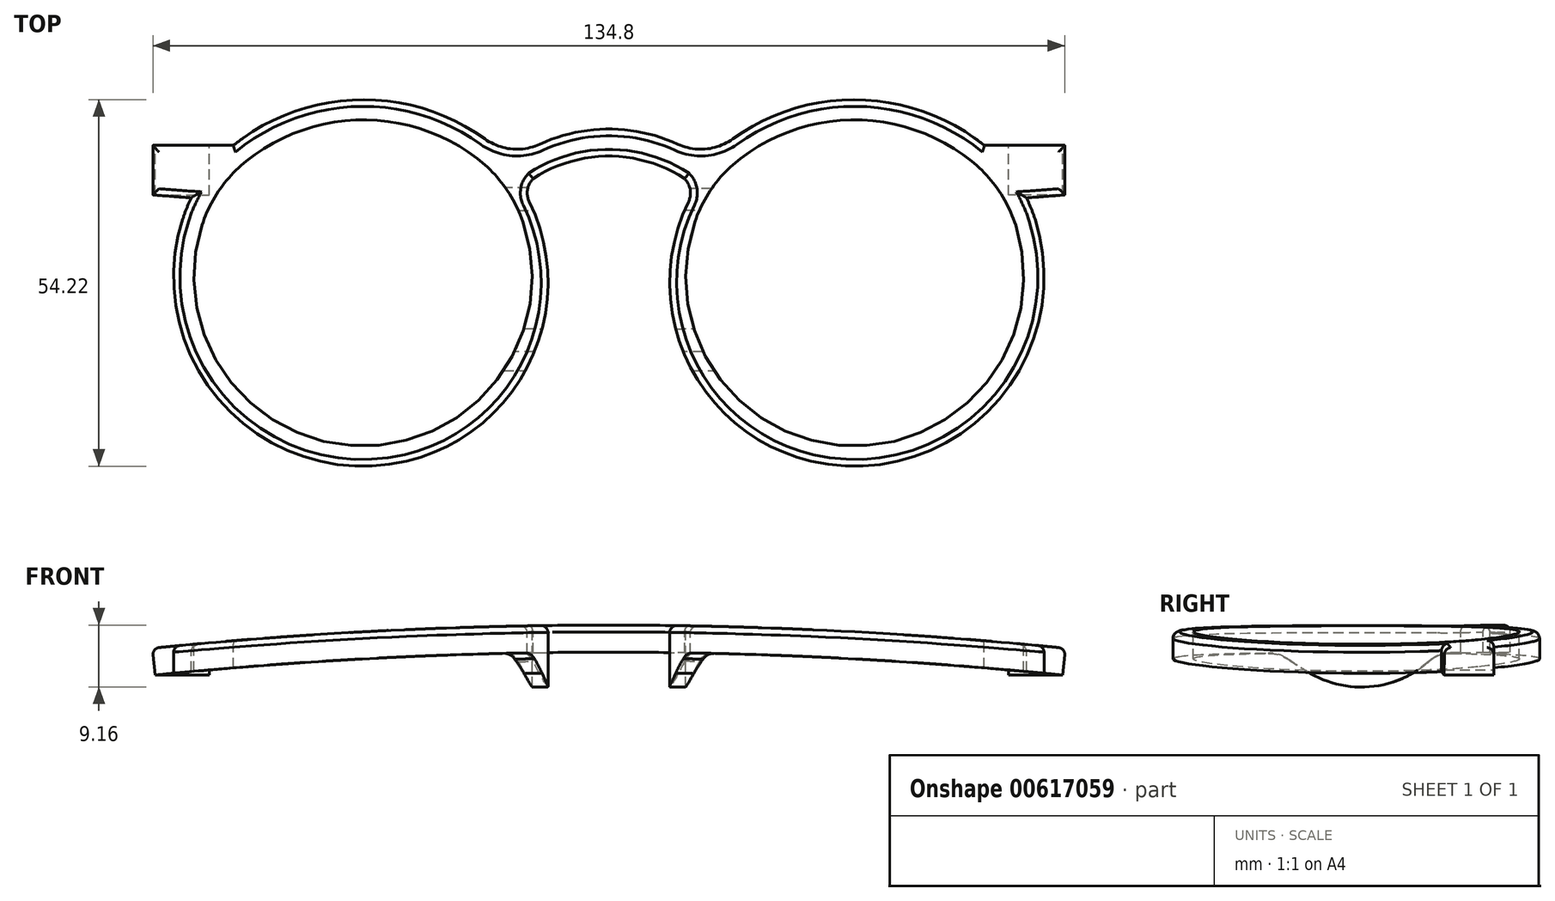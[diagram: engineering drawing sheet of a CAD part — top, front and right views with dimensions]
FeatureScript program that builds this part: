
annotation { "Feature Type Name" : "Feature", "Feature Type Description" : "" }
export const myFeature = defineFeature(function(context is Context, id is Id, definition is map)
    precondition{}
    {
        {
            var Q0;
            Q0=qCreatedBy(makeId("Front.planeOp"),FACE);
            var sketch = newSketch(context, id + "F0", { "sketchPlane" : qUnion([Q0])});
            skArc(sketch, "E0", {"start": v(0, 0) * mm, "mid": v(-67.5, 3.42) * mm, "end": v(-135, 0) * mm});
            skPoint(sketch, "E1", {"position": v(-67.5, 3.42) * mm});
            skArc(sketch, "E2.0", {"start": v(-0.4, -3.98) * mm, "mid": v(-67.5, -0.58) * mm, "end": v(-134.6, -3.98) * mm});
            skLineSegment(sketch, "E3", {"start": v(0, 0) * mm, "end": v(-0.4, -3.98) * mm});
            skLineSegment(sketch, "E4", {"start": v(-135, 0) * mm, "end": v(-134.6, -3.98) * mm});
            skSolve(sketch);
        }
        {
            var Q0;
            Q0 = qSketchRegion(id + "F0", true);
            extrude(context, id + "F1", {"entities" : qUnion([Q0]), "depth" : 56 * mm, "offsetDistance" : 25 * mm});
        }
        {
            var Q0;
            Q0=qCreatedBy(makeId("Top.planeOp"),FACE);
            var sketch = newSketch(context, id + "F2", { "sketchPlane" : qUnion([Q0])});
            skArc(sketch, "E5", {"start": v(-54.77, -18.8) * mm, "mid": v(-31.45, -52) * mm, "end": v(-7.35, -19.36) * mm});
            skArc(sketch, "E6", {"start": v(-13.88, -9.87) * mm, "mid": v(-30.88, -3.78) * mm, "end": v(-48.02, -9.47) * mm});
            skPoint(sketch, "E7.visualSharp", {"position": v(-51.95, -13.13) * mm});
            skArc(sketch, "E7.filletArc", {"start": v(-48.02, -9.47) * mm, "mid": v(-52.08, -13.63) * mm, "end": v(-54.77, -18.8) * mm});
            skPoint(sketch, "E8.visualSharp", {"position": v(-10.03, -13.63) * mm});
            skArc(sketch, "E8.filletArc", {"start": v(-7.35, -19.36) * mm, "mid": v(-9.92, -14.14) * mm, "end": v(-13.88, -9.87) * mm});
            skArc(sketch, "E9.0", {"start": v(-37.59, -54.25) * mm, "mid": v(-10.6, -46) * mm, "end": v(-4.5, -18.44) * mm});
            skArc(sketch, "E9.2", {"start": v(-12, -7.53) * mm, "mid": v(-30.42, -0.79) * mm, "end": v(-49.17, -6.58) * mm});
            skArc(sketch, "E9.3", {"start": v(-4.5, -18.44) * mm, "mid": v(-5.07, -16.85) * mm, "end": v(-5.76, -15.31) * mm});
            skLineSegment(sketch, "E10", {"start": v(0, -14.86) * mm, "end": v(-5.76, -15.31) * mm});
            skArc(sketch, "E11", {"start": v(-55.74, -15.9) * mm, "mid": v(-55.9, -39.44) * mm, "end": v(-37.59, -54.25) * mm});
            skPoint(sketch, "E12.visualSharp", {"position": v(-55.42, -15.27) * mm});
            skArc(sketch, "E12.filletArc", {"start": v(-55.74, -15.9) * mm, "mid": v(-55.47, -14.09) * mm, "end": v(-56.3, -12.46) * mm});
            skLineSegment(sketch, "E13.0", {"start": v(0, 0) * mm, "end": v(0, 0) * mm});
            skLineSegment(sketch, "E14.0", {"start": v(0, -56) * mm, "end": v(0, -56) * mm});
            skLineSegment(sketch, "E15", {"start": v(-12, -7.53) * mm, "end": v(0, -7.53) * mm});
            skLineSegment(sketch, "E16.0", {"start": v(0, 0) * mm, "end": v(-135, 0) * mm});
            skLineSegment(sketch, "E17.0", {"start": v(-135, -56) * mm, "end": v(-135, 0) * mm});
            skPoint(sketch, "E18.0", {"position": v(-67.5, -56) * mm});
            skLineSegment(sketch, "E19.0", {"start": v(0, -56) * mm, "end": v(-135, -56) * mm});
            skLineSegment(sketch, "E20.0", {"start": v(0, -56) * mm, "end": v(0, -14.86) * mm});
            skLineSegment(sketch, "E21", {"start": v(-67.5, 0) * mm, "end": v(-67.5, -56) * mm});
            skArc(sketch, "E22", {"start": v(-56.3, -12.46) * mm, "mid": v(-61.66, -9.98) * mm, "end": v(-67.5, -9.13) * mm});
            skArc(sketch, "E23", {"start": v(-57.29, -7.37) * mm, "mid": v(-62.27, -5.7) * mm, "end": v(-67.5, -5.13) * mm});
            skLineSegment(sketch, "E24.trimOffspring", {"start": v(0, -7.53) * mm, "end": v(0, 0) * mm});
            skArc(sketch, "E25", {"start": v(-57.29, -7.37) * mm, "mid": v(-53.12, -8.07) * mm, "end": v(-49.17, -6.58) * mm});
            skSolve(sketch);
        }
        {
            var Q0;
            Q0 = qSketchRegion(id + "F2", true);
            extrude(context, id + "F3", {"entities" : qUnion([Q0]), "operationType" : NewBodyOperationType.REMOVE, "oppositeDirection" : true, "depth" : 25 * mm, "offsetDistance" : 25 * mm, "hasSecondDirection" : true, "secondDirectionOppositeDirection" : false, "secondDirectionDepth" : 25 * mm});
        }
        {
            var Q0;
            Q0=makeQuery(id+"F1.opExtrude","SWEPT_BODY",BODY,{"disambiguationData":[OSD([sQuery(id+"F0.wireOp",EDGE,"E0"),sQuery(id+"F0.wireOp",EDGE,"E2.0"),sQuery(id+"F0.wireOp",EDGE,"E3"),sQuery(id+"F0.wireOp",EDGE,"E4")])]});
            var Q1;
            Q1=makeQuery(id+"F3.boolean.opBoolean","COPY",FACE,{"derivedFrom":makeQuery(id+"F3.opExtrude","SWEPT_FACE",FACE,{"disambiguationData":[OSD([sQuery(id+"F2.wireOp",EDGE,"E21")])]})});
            mirror(context, id + "F4", {"operationType" : NewBodyOperationType.ADD, "entities" : qUnion([Q0]), "mirrorPlane" : qUnion([Q1])});
        }
        {
            var Q0;
            Q0=makeQuery(id+"F3.boolean.opBoolean","INTERSECT",EDGE,{"derivedFrom":[makeQuery(id+"F1.opExtrude","SWEPT_FACE",FACE,{"disambiguationData":[OSD([sQuery(id+"F0.wireOp",EDGE,"E0")])]}),makeQuery(id+"F3.opExtrude","SWEPT_FACE",FACE,{"disambiguationData":[OSD([sQuery(id+"F2.wireOp",EDGE,"E25")])]})]});
            var Q1;
            Q1=makeQuery(id+"F3.boolean.opBoolean","INTERSECT",EDGE,{"derivedFrom":[makeQuery(id+"F1.opExtrude","SWEPT_FACE",FACE,{"disambiguationData":[OSD([sQuery(id+"F0.wireOp",EDGE,"E0")])]}),makeQuery(id+"F3.opExtrude","SWEPT_FACE",FACE,{"disambiguationData":[OSD([sQuery(id+"F2.wireOp",EDGE,"E15")])]})]});
            var Q2;
            Q2=makeQuery(id+"F1.opExtrude","SWEPT_EDGE",EDGE,{"disambiguationData":[OSD([sQuery(id+"F0.wireOp",EDGE,"E0"),sQuery(id+"F0.wireOp",EDGE,"E3")])]});
            var Q3;
            Q3=makeQuery(id+"F3.boolean.opBoolean","INTERSECT",EDGE,{"derivedFrom":[makeQuery(id+"F1.opExtrude","SWEPT_FACE",FACE,{"disambiguationData":[OSD([sQuery(id+"F0.wireOp",EDGE,"E0")])]}),makeQuery(id+"F3.opExtrude","SWEPT_FACE",FACE,{"disambiguationData":[OSD([sQuery(id+"F2.wireOp",EDGE,"E10")])]})]});
            var Q4;
            Q4=makeQuery(id+"F3.boolean.opBoolean","INTERSECT",EDGE,{"derivedFrom":[makeQuery(id+"F1.opExtrude","SWEPT_FACE",FACE,{"disambiguationData":[OSD([sQuery(id+"F0.wireOp",EDGE,"E0")])]}),makeQuery(id+"F3.opExtrude","SWEPT_FACE",FACE,{"disambiguationData":[OSD([sQuery(id+"F2.wireOp",EDGE,"E9.3")])]})]});
            var Q5;
            Q5=makeQuery(id+"F3.boolean.opBoolean","INTERSECT",EDGE,{"derivedFrom":[makeQuery(id+"F1.opExtrude","SWEPT_FACE",FACE,{"disambiguationData":[OSD([sQuery(id+"F0.wireOp",EDGE,"E0")])]}),makeQuery(id+"F3.opExtrude","SWEPT_FACE",FACE,{"disambiguationData":[OSD([sQuery(id+"F2.wireOp",EDGE,"E9.0")])]})]});
            var Q6;
            Q6=makeQuery(id+"F4.opPattern","COPY",EDGE,{"derivedFrom":makeQuery(id+"F3.boolean.opBoolean","INTERSECT",EDGE,{"derivedFrom":[makeQuery(id+"F1.opExtrude","SWEPT_FACE",FACE,{"disambiguationData":[OSD([sQuery(id+"F0.wireOp",EDGE,"E0")])]}),makeQuery(id+"F3.opExtrude","SWEPT_FACE",FACE,{"disambiguationData":[OSD([sQuery(id+"F2.wireOp",EDGE,"E12.filletArc")])]})]}),"instanceName":"1"});
            var Q7;
            Q7=makeQuery(id+"F4.opPattern","COPY",EDGE,{"derivedFrom":makeQuery(id+"F3.boolean.opBoolean","INTERSECT",EDGE,{"derivedFrom":[makeQuery(id+"F1.opExtrude","SWEPT_FACE",FACE,{"disambiguationData":[OSD([sQuery(id+"F0.wireOp",EDGE,"E0")])]}),makeQuery(id+"F3.opExtrude","SWEPT_FACE",FACE,{"disambiguationData":[OSD([sQuery(id+"F2.wireOp",EDGE,"E10")])]})]}),"instanceName":"1"});
            var Q8;
            Q8=makeQuery(id+"F4.opPattern","COPY",EDGE,{"derivedFrom":makeQuery(id+"F1.opExtrude","SWEPT_EDGE",EDGE,{"disambiguationData":[OSD([sQuery(id+"F0.wireOp",EDGE,"E0"),sQuery(id+"F0.wireOp",EDGE,"E3")])]}),"instanceName":"1"});
            var Q9;
            Q9=makeQuery(id+"F4.opPattern","COPY",EDGE,{"derivedFrom":makeQuery(id+"F3.boolean.opBoolean","INTERSECT",EDGE,{"derivedFrom":[makeQuery(id+"F1.opExtrude","SWEPT_FACE",FACE,{"disambiguationData":[OSD([sQuery(id+"F0.wireOp",EDGE,"E0")])]}),makeQuery(id+"F3.opExtrude","SWEPT_FACE",FACE,{"disambiguationData":[OSD([sQuery(id+"F2.wireOp",EDGE,"E15")])]})]}),"instanceName":"1"});
            fillet(context, id + "F5", {"entities" : qUnion([Q0, Q1, Q2, Q3, Q4, Q5, Q6, Q7, Q8, Q9]), "radius" : 1 * mm, "tangentPropagation" : true, "allowEdgeOverflow" : false});
        }
        {
            var Q0;
            {var subQ0=makeQuery(id+"F3.boolean.opBoolean","INTERSECT",EDGE,{"derivedFrom":[makeQuery(id+"F1.opExtrude","SWEPT_FACE",FACE,{"disambiguationData":[OSD([sQuery(id+"F0.wireOp",EDGE,"E0")])]}),makeQuery(id+"F3.opExtrude","SWEPT_FACE",FACE,{"disambiguationData":[OSD([sQuery(id+"F2.wireOp",EDGE,"E22")])]})]});Q0=makeQuery(id+"F4.boolean.opBoolean","MERGE",EDGE,{"derivedFrom":[subQ0,makeQuery(id+"F4.opPattern","COPY",EDGE,{"derivedFrom":subQ0,"instanceName":"1"})]});}
            fillet(context, id + "F6", {"entities" : qUnion([Q0]), "radius" : 1 * mm, "tangentPropagation" : true, "allowEdgeOverflow" : false});
        }
        {
            var Q0;
            Q0=qCreatedBy(makeId("Top.planeOp"),FACE);
            var sketch = newSketch(context, id + "F7", { "sketchPlane" : qUnion([Q0])});
            skArc(sketch, "E26.0", {"start": v(-127.65, -19.36) * mm, "mid": v(-103.55, -52) * mm, "end": v(-80.23, -18.8) * mm});
            skArc(sketch, "E27.0", {"start": v(-97.41, -54.25) * mm, "mid": v(-79.1, -39.44) * mm, "end": v(-79.26, -15.9) * mm});
            skArc(sketch, "E28.0", {"start": v(-78.7, -12.46) * mm, "mid": v(-79.53, -14.09) * mm, "end": v(-79.26, -15.9) * mm});
            skArc(sketch, "E29.0", {"start": v(-80.23, -18.8) * mm, "mid": v(-82.92, -13.63) * mm, "end": v(-86.98, -9.47) * mm});
            skLineSegment(sketch, "E30", {"start": v(-79.26, -15.9) * mm, "end": v(-81.5, -15.9) * mm});
            skLineSegment(sketch, "E31", {"start": v(-82.08, -39.3) * mm, "end": v(-79.04, -39.3) * mm});
            skArc(sketch, "E32.0", {"start": v(-56.3, -12.46) * mm, "mid": v(-67.5, -9.13) * mm, "end": v(-78.7, -12.46) * mm});
            skArc(sketch, "E33.0", {"start": v(-57.29, -7.37) * mm, "mid": v(-67.5, -5.13) * mm, "end": v(-77.71, -7.37) * mm});
            skLineSegment(sketch, "E34", {"start": v(-67.5, -9.13) * mm, "end": v(-67.5, -5.13) * mm});
            skArc(sketch, "E35.MirrorCS", {"start": v(-54.77, -18.8) * mm, "mid": v(-52.08, -13.63) * mm, "end": v(-48.02, -9.47) * mm});
            skLineSegment(sketch, "E36.MirrorCS", {"start": v(-52.92, -39.3) * mm, "end": v(-55.96, -39.3) * mm});
            skArc(sketch, "E37.MirrorCS", {"start": v(-56.3, -12.46) * mm, "mid": v(-55.47, -14.09) * mm, "end": v(-55.74, -15.9) * mm});
            skLineSegment(sketch, "E38.MirrorCS", {"start": v(-55.74, -15.9) * mm, "end": v(-53.5, -15.9) * mm});
            skArc(sketch, "E39.MirrorCS", {"start": v(-37.59, -54.25) * mm, "mid": v(-55.9, -39.44) * mm, "end": v(-55.74, -15.9) * mm});
            skArc(sketch, "E40.MirrorCS", {"start": v(-7.35, -19.36) * mm, "mid": v(-31.45, -52) * mm, "end": v(-54.77, -18.8) * mm});
            skSolve(sketch);
        }
        {
            var Q0;
            Q0 = qSketchRegion(id + "F7", true);
            extrude(context, id + "F8", {"entities" : qUnion([Q0]), "operationType" : NewBodyOperationType.ADD, "oppositeDirection" : true, "depth" : 10 * mm, "offsetDistance" : 25 * mm});
        }
        {
            var Q0;
            {var subQ0=makeQuery(id+"F3.boolean.opBoolean","INTERSECT",EDGE,{"derivedFrom":[makeQuery(id+"F1.opExtrude","SWEPT_FACE",FACE,{"disambiguationData":[OSD([sQuery(id+"F0.wireOp",EDGE,"E2.0")])]}),makeQuery(id+"F3.opExtrude","SWEPT_FACE",FACE,{"disambiguationData":[OSD([sQuery(id+"F2.wireOp",EDGE,"E22")])]})]});Q0=makeQuery(id+"F4.boolean.opBoolean","MERGE",EDGE,{"derivedFrom":[subQ0,makeQuery(id+"F4.opPattern","COPY",EDGE,{"derivedFrom":subQ0,"instanceName":"1"})]});}
            cPoint(context, id + "F9", {"entities" : qUnion([Q0]), "parameter" : 0.5});
        }
        {
            var Q0;
            {var subQ0=makeQuery(id+"F3.boolean.opBoolean","INTERSECT",EDGE,{"derivedFrom":[makeQuery(id+"F1.opExtrude","SWEPT_FACE",FACE,{"disambiguationData":[OSD([sQuery(id+"F0.wireOp",EDGE,"E2.0")])]}),makeQuery(id+"F3.opExtrude","SWEPT_FACE",FACE,{"disambiguationData":[OSD([sQuery(id+"F2.wireOp",EDGE,"E23")])]})]});Q0=makeQuery(id+"F4.boolean.opBoolean","MERGE",EDGE,{"derivedFrom":[subQ0,makeQuery(id+"F4.opPattern","COPY",EDGE,{"derivedFrom":subQ0,"instanceName":"1"})]});}
            cPoint(context, id + "F10", {"entities" : qUnion([Q0]), "parameter" : 0.5});
        }
        {
            var Q0;
            {var subQ0=makeQuery(id+"F3.opExtrude","SWEPT_FACE",FACE,{"disambiguationData":[OSD([sQuery(id+"F2.wireOp",EDGE,"E22")])]});var subQ1=makeQuery(id+"F3.boolean.opBoolean","COPY",FACE,{"derivedFrom":subQ0});var subQ2=makeQuery(id+"F3.boolean.opBoolean","INTERSECT",EDGE,{"derivedFrom":[makeQuery(id+"F1.opExtrude","SWEPT_FACE",FACE,{"disambiguationData":[OSD([sQuery(id+"F0.wireOp",EDGE,"E0")])]}),subQ0]});Q0=makeQuery(id+"F6.opFillet","BLEND_EDGE",EDGE,{"blendedFrom":[makeQuery(id+"F4.boolean.opBoolean","MERGE",EDGE,{"derivedFrom":[subQ2,makeQuery(id+"F4.opPattern","COPY",EDGE,{"derivedFrom":subQ2,"instanceName":"1"})]}),makeQuery(id+"F4.boolean.opBoolean","MERGE",FACE,{"derivedFrom":[subQ1,makeQuery(id+"F4.opPattern","COPY",FACE,{"derivedFrom":subQ1,"instanceName":"1"})]})],"blendedInto":[makeQuery(id+"F4.boolean.opBoolean","MERGE",FACE,{"derivedFrom":[subQ1,makeQuery(id+"F4.opPattern","COPY",FACE,{"derivedFrom":subQ1,"instanceName":"1"})]})]});}
            cPoint(context, id + "F11", {"entities" : qUnion([Q0]), "parameter" : 0.5});
        }
        {
            var Q0;
            Q0 = qCreatedBy(id + "F9" ,VERTEX);
            var Q1;
            Q1 = qCreatedBy(id + "F10" ,VERTEX);
            var Q2;
            Q2 = qCreatedBy(id + "F11" ,VERTEX);
            cPlane(context, id + "F12", {"entities" : qUnion([Q0, Q1, Q2]), "cplaneType" : CPlaneType.THREE_POINT, "offset" : 25 * mm, "width" : 150 * mm, "height" : 150 * mm});
        }
        {
            var Q0;
            Q0=makeQuery(id+"F3.boolean.opBoolean","COPY",FACE,{"derivedFrom":makeQuery(id+"F3.opExtrude","SWEPT_FACE",FACE,{"disambiguationData":[OSD([sQuery(id+"F2.wireOp",EDGE,"E15")])]})});
            var sketch = newSketch(context, id + "F13", { "sketchPlane" : qUnion([Q0])});
            skLineSegment(sketch, "E41.0", {"start": v(0.1, -1) * mm, "end": v(0.4, -3.98) * mm});
            skLineSegment(sketch, "E42", {"start": v(0.4, -3.98) * mm, "end": v(8.4, -3.98) * mm});
            skArc(sketch, "E43.0", {"start": v(0.4, -3.98) * mm, "mid": v(6.2, -3.42) * mm, "end": v(12, -2.9) * mm});
            skLineSegment(sketch, "E44", {"start": v(8.4, -3.98) * mm, "end": v(8.4, -3.22) * mm});
            skSolve(sketch);
        }
        {
            var Q0;
            Q0 = qSketchRegion(id + "F13", true);
            var Q1;
            Q1=makeQuery(id+"F3.boolean.opBoolean","INTERSECT",VERTEX,{"derivedFrom":[makeQuery(id+"F1.opExtrude","SWEPT_FACE",FACE,{"disambiguationData":[OSD([sQuery(id+"F0.wireOp",EDGE,"E2.0")])]}),makeQuery(id+"F1.opExtrude","SWEPT_FACE",FACE,{"disambiguationData":[OSD([sQuery(id+"F0.wireOp",EDGE,"E3")])]}),makeQuery(id+"F3.opExtrude","SWEPT_FACE",FACE,{"disambiguationData":[OSD([sQuery(id+"F2.wireOp",EDGE,"E10")])]})]});
            extrude(context, id + "F14", {"entities" : qUnion([Q0]), "endBound" : BoundingType.UP_TO_VERTEX, "oppositeDirection" : true, "depth" : 25 * mm, "endBoundEntityVertex" : qUnion([Q1]), "offsetDistance" : 25 * mm});
        }
        {
            var Q0;
            Q0=makeQuery(id+"F14.opExtrude","SWEPT_BODY",BODY,{"disambiguationData":[OSD([sQuery(id+"F13.wireOp",EDGE,"E42"),sQuery(id+"F13.wireOp",EDGE,"E43.0"),sQuery(id+"F13.wireOp",EDGE,"E44")])]});
            var Q1;
            Q1=qCreatedBy(id+"F12.planeOp",FACE);
            mirror(context, id + "F15", {"entities" : qUnion([Q0]), "mirrorPlane" : qUnion([Q1])});
        }
        {
            var Q0;
            Q0=makeQuery(id+"F8.opExtrude","CAP_EDGE",EDGE,{"disambiguationData":[OSD([sQuery(id+"F7.wireOp",EDGE,"E36.MirrorCS")])],"isStart":false});
            var Q1;
            Q1=makeQuery(id+"F8.opExtrude","CAP_EDGE",EDGE,{"disambiguationData":[OSD([sQuery(id+"F7.wireOp",EDGE,"E31")])],"isStart":false});
            fillet(context, id + "F16", {"entities" : qUnion([Q0, Q1]), "radius" : 50 * mm, "rho" : 0.5, "crossSection" : FilletCrossSection.CONIC, "allowEdgeOverflow" : false});
        }
        {
            var Q0;
            Q0=makeQuery(id+"F16.opFillet","BLEND_EDGE",EDGE,{"blendedFrom":[makeQuery(id+"F8.opExtrude","CAP_EDGE",EDGE,{"disambiguationData":[OSD([sQuery(id+"F7.wireOp",EDGE,"E31")])],"isStart":false}),makeQuery(id+"F8.opExtrude","SWEPT_FACE",FACE,{"disambiguationData":[OSD([sQuery(id+"F7.wireOp",EDGE,"E30")])]})],"blendedInto":[makeQuery(id+"F8.opExtrude","SWEPT_FACE",FACE,{"disambiguationData":[OSD([sQuery(id+"F7.wireOp",EDGE,"E30")])]})]});
            var Q1;
            Q1=makeQuery(id+"F16.opFillet","BLEND_EDGE",EDGE,{"blendedFrom":[makeQuery(id+"F8.opExtrude","CAP_EDGE",EDGE,{"disambiguationData":[OSD([sQuery(id+"F7.wireOp",EDGE,"E36.MirrorCS")])],"isStart":false}),makeQuery(id+"F8.opExtrude","SWEPT_FACE",FACE,{"disambiguationData":[OSD([sQuery(id+"F7.wireOp",EDGE,"E38.MirrorCS")])]})],"blendedInto":[makeQuery(id+"F8.opExtrude","SWEPT_FACE",FACE,{"disambiguationData":[OSD([sQuery(id+"F7.wireOp",EDGE,"E38.MirrorCS")])]})]});
            fillet(context, id + "F17", {"entities" : qUnion([Q0, Q1]), "radius" : 15 * mm, "tangentPropagation" : true, "allowEdgeOverflow" : false});
        }
        {
            var Q0;
            {var subQ0=makeQuery(id+"F1.opExtrude","SWEPT_FACE",FACE,{"disambiguationData":[OSD([sQuery(id+"F0.wireOp",EDGE,"E2.0")])]});Q0=makeQuery(id+"F17.opFillet","BLEND_EDGE",EDGE,{"blendedFrom":[makeQuery(id+"F16.opFillet","BLEND_EDGE",EDGE,{"blendedFrom":[makeQuery(id+"F8.opExtrude","CAP_EDGE",EDGE,{"disambiguationData":[OSD([sQuery(id+"F7.wireOp",EDGE,"E31")])],"isStart":false}),makeQuery(id+"F8.opExtrude","SWEPT_FACE",FACE,{"disambiguationData":[OSD([sQuery(id+"F7.wireOp",EDGE,"E30")])]})],"blendedInto":[makeQuery(id+"F8.opExtrude","SWEPT_FACE",FACE,{"disambiguationData":[OSD([sQuery(id+"F7.wireOp",EDGE,"E30")])]})]}),makeQuery(id+"F4.boolean.opBoolean","MERGE",FACE,{"derivedFrom":[subQ0,makeQuery(id+"F4.opPattern","COPY",FACE,{"derivedFrom":subQ0,"instanceName":"1"})]})],"blendedInto":[makeQuery(id+"F4.boolean.opBoolean","MERGE",FACE,{"derivedFrom":[subQ0,makeQuery(id+"F4.opPattern","COPY",FACE,{"derivedFrom":subQ0,"instanceName":"1"})]})]});}
            var Q1;
            {var subQ0=makeQuery(id+"F1.opExtrude","SWEPT_FACE",FACE,{"disambiguationData":[OSD([sQuery(id+"F0.wireOp",EDGE,"E2.0")])]});Q1=makeQuery(id+"F16.opFillet","BLEND_EDGE",EDGE,{"blendedFrom":[makeQuery(id+"F8.opExtrude","CAP_EDGE",EDGE,{"disambiguationData":[OSD([sQuery(id+"F7.wireOp",EDGE,"E36.MirrorCS")])],"isStart":false}),makeQuery(id+"F4.boolean.opBoolean","MERGE",FACE,{"derivedFrom":[subQ0,makeQuery(id+"F4.opPattern","COPY",FACE,{"derivedFrom":subQ0,"instanceName":"1"})]})],"blendedInto":[makeQuery(id+"F4.boolean.opBoolean","MERGE",FACE,{"derivedFrom":[subQ0,makeQuery(id+"F4.opPattern","COPY",FACE,{"derivedFrom":subQ0,"instanceName":"1"})]})]});}
            var Q2;
            {var subQ0=makeQuery(id+"F1.opExtrude","SWEPT_FACE",FACE,{"disambiguationData":[OSD([sQuery(id+"F0.wireOp",EDGE,"E2.0")])]});Q2=makeQuery(id+"F16.opFillet","BLEND_EDGE",EDGE,{"blendedFrom":[makeQuery(id+"F8.opExtrude","CAP_EDGE",EDGE,{"disambiguationData":[OSD([sQuery(id+"F7.wireOp",EDGE,"E31")])],"isStart":false}),makeQuery(id+"F4.boolean.opBoolean","MERGE",FACE,{"derivedFrom":[subQ0,makeQuery(id+"F4.opPattern","COPY",FACE,{"derivedFrom":subQ0,"instanceName":"1"})]})],"blendedInto":[makeQuery(id+"F4.boolean.opBoolean","MERGE",FACE,{"derivedFrom":[subQ0,makeQuery(id+"F4.opPattern","COPY",FACE,{"derivedFrom":subQ0,"instanceName":"1"})]})]});}
            fillet(context, id + "F18", {"entities" : qUnion([Q0, Q1, Q2]), "radius" : 5 * mm, "tangentPropagation" : true, "allowEdgeOverflow" : false});
        }
        {
            var Q0;
            {var subQ0=makeQuery(id+"F1.opExtrude","SWEPT_FACE",FACE,{"disambiguationData":[OSD([sQuery(id+"F0.wireOp",EDGE,"E2.0")])]});Q0=makeQuery(id+"F17.opFillet","BLEND_EDGE",EDGE,{"blendedFrom":[makeQuery(id+"F16.opFillet","BLEND_EDGE",EDGE,{"blendedFrom":[makeQuery(id+"F8.opExtrude","CAP_EDGE",EDGE,{"disambiguationData":[OSD([sQuery(id+"F7.wireOp",EDGE,"E36.MirrorCS")])],"isStart":false}),makeQuery(id+"F8.opExtrude","SWEPT_FACE",FACE,{"disambiguationData":[OSD([sQuery(id+"F7.wireOp",EDGE,"E38.MirrorCS")])]})],"blendedInto":[makeQuery(id+"F8.opExtrude","SWEPT_FACE",FACE,{"disambiguationData":[OSD([sQuery(id+"F7.wireOp",EDGE,"E38.MirrorCS")])]})]}),makeQuery(id+"F4.boolean.opBoolean","MERGE",FACE,{"derivedFrom":[subQ0,makeQuery(id+"F4.opPattern","COPY",FACE,{"derivedFrom":subQ0,"instanceName":"1"})]})],"blendedInto":[makeQuery(id+"F4.boolean.opBoolean","MERGE",FACE,{"derivedFrom":[subQ0,makeQuery(id+"F4.opPattern","COPY",FACE,{"derivedFrom":subQ0,"instanceName":"1"})]})]});}
            fillet(context, id + "F19", {"entities" : qUnion([Q0]), "radius" : 4.7 * mm, "tangentPropagation" : true, "allowEdgeOverflow" : false});
        }
    });
